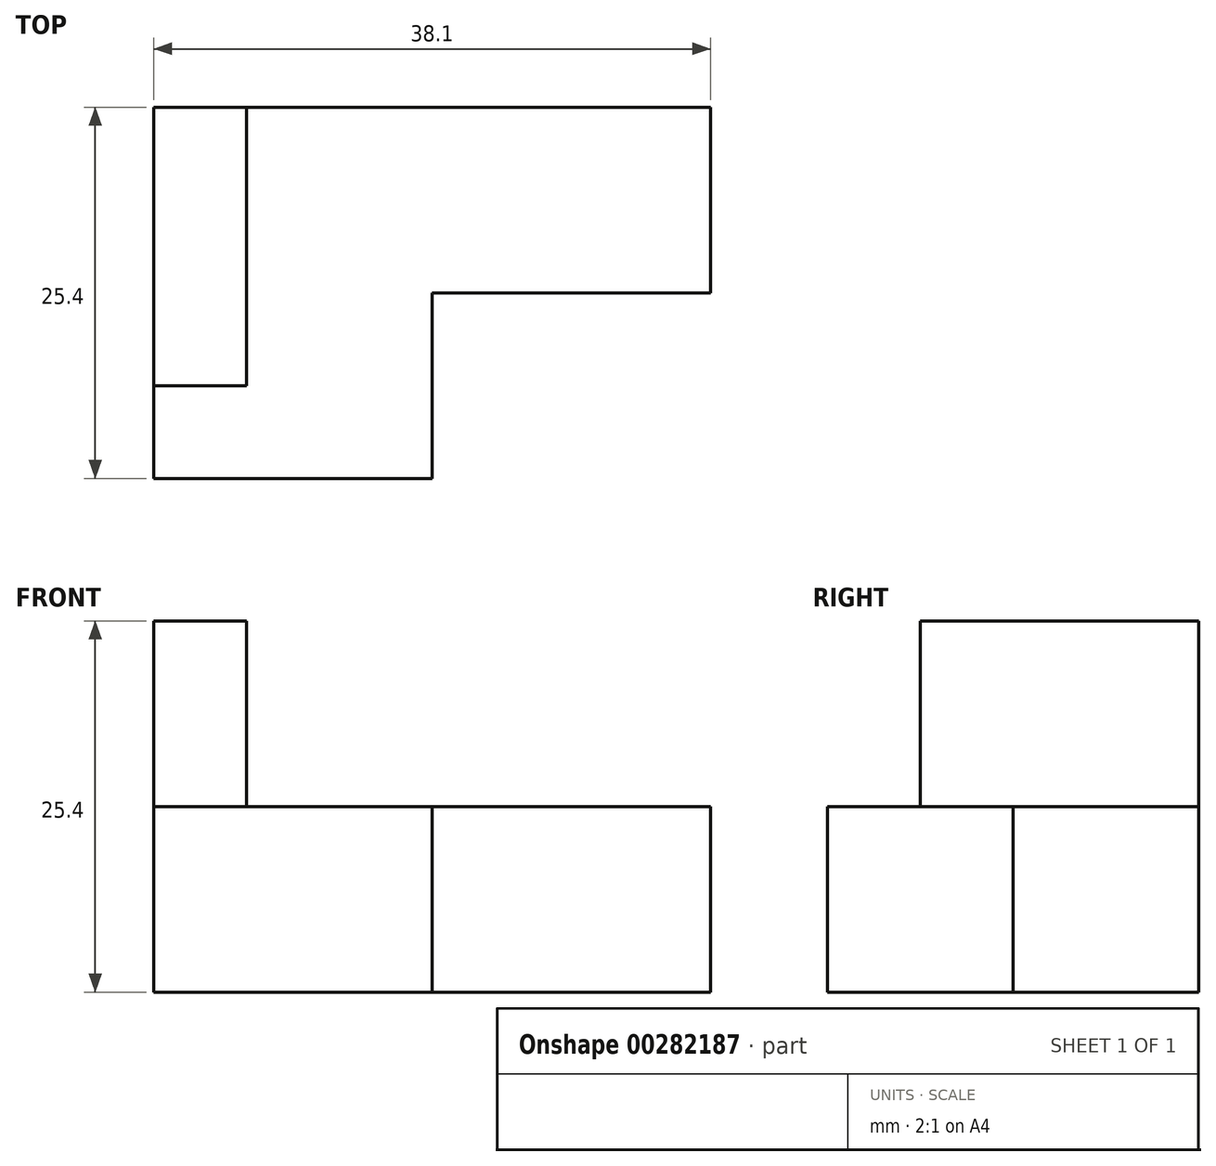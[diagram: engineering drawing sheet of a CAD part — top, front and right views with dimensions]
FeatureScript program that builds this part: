
annotation { "Feature Type Name" : "Feature", "Feature Type Description" : "" }
export const myFeature = defineFeature(function(context is Context, id is Id, definition is map)
    precondition{}
    {
        {
            var Q0;
            Q0=qCreatedBy(makeId("Top.planeOp"),FACE);
            var sketch = newSketch(context, id + "F0", { "sketchPlane" : qUnion([Q0])});
            skLineSegment(sketch, "E0", {"start": v(0, 0) * mm, "end": v(0, -25.4) * mm});
            skLineSegment(sketch, "E1", {"start": v(0, -25.4) * mm, "end": v(19.05, -25.4) * mm});
            skLineSegment(sketch, "E2", {"start": v(19.05, -25.4) * mm, "end": v(19.05, -12.7) * mm});
            skLineSegment(sketch, "E3", {"start": v(19.05, -12.7) * mm, "end": v(38.1, -12.7) * mm});
            skLineSegment(sketch, "E4", {"start": v(38.1, -12.7) * mm, "end": v(38.1, 0) * mm});
            skLineSegment(sketch, "E5", {"start": v(38.1, 0) * mm, "end": v(0, 0) * mm});
            skSolve(sketch);
        }
        {
            var Q0;
            Q0=makeQuery(id+"F0.imprint","IMPRINT",FACE,{"disambiguationData":[TD([[makeQuery(id+"F0.imprint","IMPRINT",EDGE,{"derivedFrom":sQuery(id+"F0.wireOp",EDGE,"E0")}),1.0]])]});
            extrude(context, id + "F1", {"entities" : qUnion([Q0]), "depth" : 12.7 * mm});
        }
        {
            var Q0;
            Q0=makeQuery(id+"F1.opExtrude","CAP_FACE",FACE,{"disambiguationData":[OSD([sQuery(id+"F0.wireOp",EDGE,"E0"),sQuery(id+"F0.wireOp",EDGE,"E1"),sQuery(id+"F0.wireOp",EDGE,"E2"),sQuery(id+"F0.wireOp",EDGE,"E3"),sQuery(id+"F0.wireOp",EDGE,"E4"),sQuery(id+"F0.wireOp",EDGE,"E5")])],"isStart":false});
            var sketch = newSketch(context, id + "F2", { "sketchPlane" : qUnion([Q0])});
            skLineSegment(sketch, "E6", {"start": v(0, 0) * mm, "end": v(6.35, 0) * mm});
            skLineSegment(sketch, "E7", {"start": v(6.35, 0) * mm, "end": v(6.35, -19.05) * mm});
            skLineSegment(sketch, "E8", {"start": v(6.35, -19.05) * mm, "end": v(0, -19.05) * mm});
            skLineSegment(sketch, "E9", {"start": v(0, -19.05) * mm, "end": v(0, 0) * mm});
            skSolve(sketch);
        }
        {
            var Q0;
            Q0=makeQuery(id+"F2.imprint","IMPRINT",FACE,{"disambiguationData":[TD([[makeQuery(id+"F2.imprint","IMPRINT",EDGE,{"derivedFrom":sQuery(id+"F2.wireOp",EDGE,"E6")}),1.0]])]});
            extrude(context, id + "F3", {"entities" : qUnion([Q0]), "operationType" : NewBodyOperationType.ADD, "depth" : 12.7 * mm});
        }
    });
